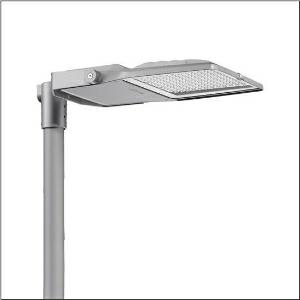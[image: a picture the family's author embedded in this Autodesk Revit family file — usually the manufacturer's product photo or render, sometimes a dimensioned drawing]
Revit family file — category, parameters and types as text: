
# Revit family: floodlight_fl_21_midi___pl33t_5xa7782f2f3a_5b33
name_source: partatom
category: Lighting Fixtures
units: mm (PartAtom-declared; Revit-internal decimal feet)

## family parameters
Cut with Voids When Loaded = No
Host = Face
Light Source = No
Part Type = Normal
Room Calculation Point = No
Round Connector Dimension = Use Diameter
Shared = No

## types (1)
- --- (1 x LED, 35350 lm, 270.2 W, 3000K)
    Apparent Load = 270 VA
    CIE Flux Codes = 26 75 99 100 100
    Color Rendering = 70
    Color Temperature = 3000K
    Default Elevation = 1800 mm
    Description = Floodlight FL 21 midi, floodlight, primary light control with lens, of PMMA, primary optical cover: protective disc, of toughened safety glass, transparent, light distribution: PL33T, light emission: direct distribution, installation type: surface-mounted, LED, High Power LED, rated luminous flux: 35.350lm, luminous efficacy: 130lm/W, light colour: 730, colour temperature: 3000K, control gear: ECG iQ, control: optimised constant luminous flux control (CLO 2.0), Desk-Remote (wireless, voltage-free reading and setting of iQ features in the workshop via application-optimized NFC function/RFID function), Smart-Wire, Night-Set, Temp-Guard, Auto-Match, Street-Remote, with terminal, 6-pole, mains connection: 220..240V, AC, 50/60Hz, start of lifetime: 270W, end of lifetime: 286W, reduction: 130W, luminaire housing, of diecast aluminium, powder-coated, Siteco® metallic grey (DB 702S), corrosivity category C5 according to DIN EN ISO 12944, mast bracket, of steel, galvanised, powder-coated, Siteco® metallic grey (DB 702S), protection rating (complete): IP66, insulation class (complete): insulation class II (safety insulation), certification: CE, protection symbol: D, impact resistance: IK08, permissible operating ambient temperature: -40..+40°C, permissible operating ambient temperature for outdoor applications: -40..+50°C, standard: DIN EN 12944, packaging unit: 1 piece

Light Distribution: PL33T
    Height = 76 mm
    Lamp = 1 x LED
    Lamp Light Flux = 35350 lm
    Lamp Power = 270.2 W
    Lamp count = 1
    Length = 657 mm
    Luminous efficacy = 131 lm/W
    Manufacturer = Siteco
    ModVariant = No
    Model = 5XA7782F2F3A
    Number of Poles = 1
    OnlyDefault = Yes
    Power Factor = 1
    Product Name = Floodlight FL 21 midi | PL33T
    Product group = floodlight | pylon top
    ProductGroupID = 6101
    Protection Class = Protection class II
    Protection Degree = IP 66
    RLX_Detail_Level = 1
    RlxData = <blob elided: 153373 chars, md5=007bba44>
    Socket = socket
    Standby Power = 0 W
    System Light Flux = 35350 lm
    System Power = 270 W
    Type Comments = factory setting: luminous flux: 100 % | dim-lin: 254 | 620 mA
    Type Image = l_1007123.jpg
    URL = http://relux.com
    VarID = @adj_011979
    Voltage = 0 V
    Weight = 0.00 kg
    Width = 442 mm

## geometry (parser evidence)
native form markers: Blend x4, Sweep x10
no freeform markers — native parametric forms only
